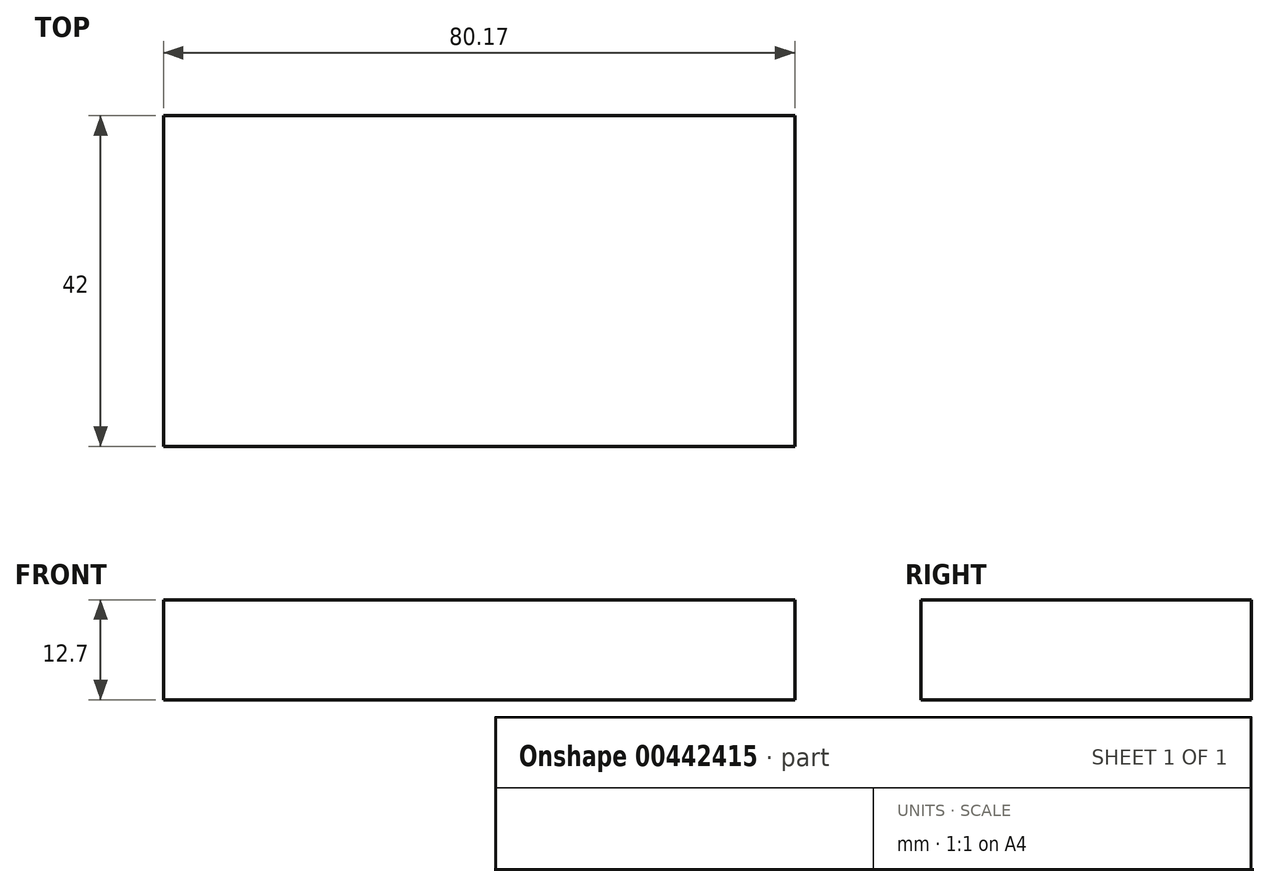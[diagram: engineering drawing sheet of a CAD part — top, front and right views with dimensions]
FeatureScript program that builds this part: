
annotation { "Feature Type Name" : "Feature", "Feature Type Description" : "" }
export const myFeature = defineFeature(function(context is Context, id is Id, definition is map)
    precondition{}
    {
        {
            var Q0;
            Q0=qCreatedBy(makeId("Top.planeOp"),FACE);
            var sketch = newSketch(context, id + "F0", { "sketchPlane" : qUnion([Q0])});
            skLineSegment(sketch, "E0.bottom", {"start": v(-40.82, -29.08) * mm, "end": v(39.35, -29.08) * mm});
            skLineSegment(sketch, "E0.top", {"start": v(-40.82, 12.92) * mm, "end": v(39.35, 12.92) * mm});
            skLineSegment(sketch, "E0.left", {"start": v(-40.82, -29.08) * mm, "end": v(-40.82, 12.92) * mm});
            skLineSegment(sketch, "E0.right", {"start": v(39.35, -29.08) * mm, "end": v(39.35, 12.92) * mm});
            skSolve(sketch);
        }
        {
            var Q0;
            Q0=makeQuery(id+"F0.imprint","IMPRINT",FACE,{"disambiguationData":[TD([[makeQuery(id+"F0.imprint","IMPRINT",EDGE,{"derivedFrom":sQuery(id+"F0.wireOp",EDGE,"E0.bottom")}),1.0]])]});
            extrude(context, id + "F1", {"entities" : qUnion([Q0]), "depth" : 12.7 * mm});
        }
    });
